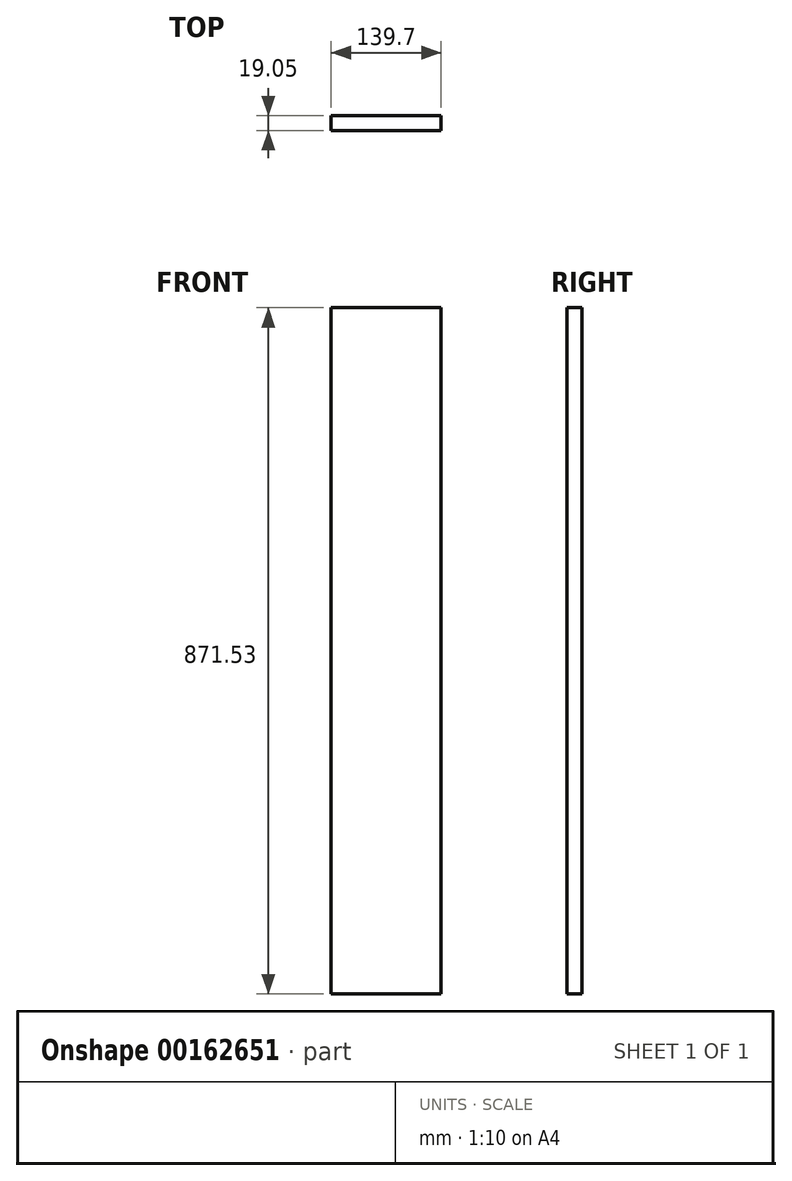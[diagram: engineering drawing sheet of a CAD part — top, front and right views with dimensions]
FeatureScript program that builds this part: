
annotation { "Feature Type Name" : "Feature", "Feature Type Description" : "" }
export const myFeature = defineFeature(function(context is Context, id is Id, definition is map)
    precondition{}
    {
        {
            var Q0;
            Q0=qCreatedBy(makeId("Front.planeOp"),FACE);
            var sketch = newSketch(context, id + "F0", { "sketchPlane" : qUnion([Q0])});
            skLineSegment(sketch, "E0.bottom", {"start": v(-92.25, 617.05) * mm, "end": v(47.45, 617.05) * mm});
            skLineSegment(sketch, "E0.top", {"start": v(-92.25, -254.48) * mm, "end": v(47.45, -254.48) * mm});
            skLineSegment(sketch, "E0.left", {"start": v(-92.25, 617.05) * mm, "end": v(-92.25, -254.48) * mm});
            skLineSegment(sketch, "E0.right", {"start": v(47.45, 617.05) * mm, "end": v(47.45, -254.48) * mm});
            skSolve(sketch);
        }
        {
            var Q0;
            Q0 = qSketchRegion(id + "F0", true);
            extrude(context, id + "F1", {"entities" : qUnion([Q0]), "depth" : 19.05 * mm});
        }
    });
